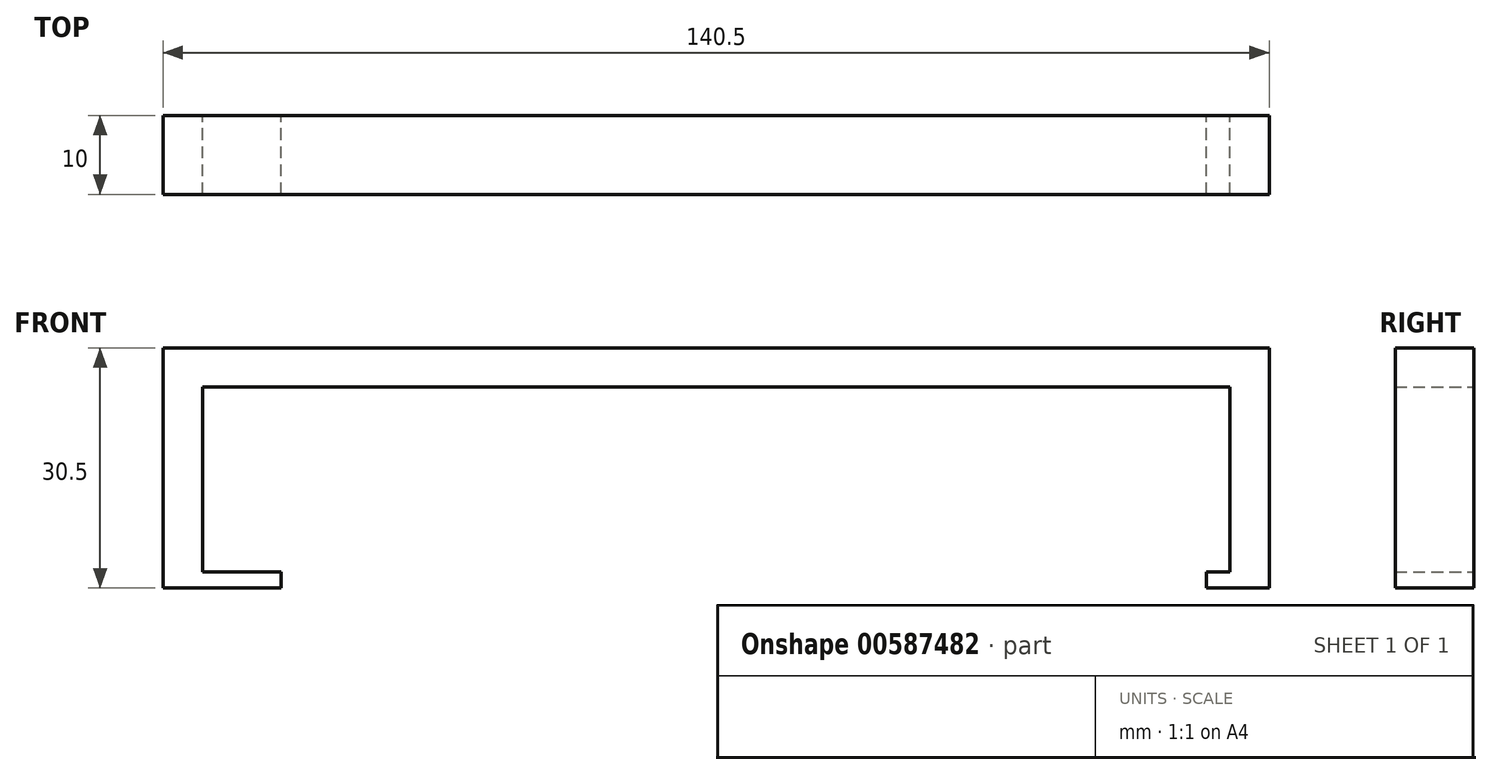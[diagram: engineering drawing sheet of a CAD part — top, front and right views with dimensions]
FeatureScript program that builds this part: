
annotation { "Feature Type Name" : "Feature", "Feature Type Description" : "" }
export const myFeature = defineFeature(function(context is Context, id is Id, definition is map)
    precondition{}
    {
        {
            var Q0;
            Q0=qCreatedBy(makeId("Front.planeOp"),FACE);
            var sketch = newSketch(context, id + "F0", { "sketchPlane" : qUnion([Q0])});
            skLineSegment(sketch, "E0.bottom", {"start": v(-65.25, 2.5) * mm, "end": v(65.25, 2.5) * mm});
            skLineSegment(sketch, "E0.top", {"start": v(-65.25, -2.5) * mm, "end": v(65.25, -2.5) * mm});
            skLineSegment(sketch, "E0.left", {"start": v(-65.25, 2.5) * mm, "end": v(-65.25, -2.5) * mm});
            skLineSegment(sketch, "E0.right", {"start": v(65.25, 2.5) * mm, "end": v(65.25, -2.5) * mm});
            skPoint(sketch, "E0.middle", {"position": v(0, 0) * mm});
            skLineSegment(sketch, "E1.top", {"start": v(65.27, -26) * mm, "end": v(70.25, -26) * mm});
            skLineSegment(sketch, "E2.bottom", {"start": v(70.25, -26) * mm, "end": v(62.25, -26) * mm});
            skLineSegment(sketch, "E2.top", {"start": v(70.25, -28) * mm, "end": v(62.25, -28) * mm});
            skLineSegment(sketch, "E2.left", {"start": v(70.25, -26) * mm, "end": v(70.25, -28) * mm});
            skLineSegment(sketch, "E2.right", {"start": v(62.25, -26) * mm, "end": v(62.25, -28) * mm});
            skLineSegment(sketch, "E3.bottom", {"start": v(-70.25, -26) * mm, "end": v(-55.25, -26) * mm});
            skLineSegment(sketch, "E3.top", {"start": v(-70.25, -28) * mm, "end": v(-55.25, -28) * mm});
            skLineSegment(sketch, "E3.left", {"start": v(-70.25, -26) * mm, "end": v(-70.25, -28) * mm});
            skLineSegment(sketch, "E3.right", {"start": v(-55.25, -26) * mm, "end": v(-55.25, -28) * mm});
            skLineSegment(sketch, "E4.bottom", {"start": v(-65.25, 2.5) * mm, "end": v(-70.25, 2.5) * mm});
            skLineSegment(sketch, "E4.top", {"start": v(-65.25, -26) * mm, "end": v(-70.25, -26) * mm});
            skLineSegment(sketch, "E4.left", {"start": v(-65.25, 2.5) * mm, "end": v(-65.25, -26) * mm});
            skLineSegment(sketch, "E4.right", {"start": v(-70.25, 2.5) * mm, "end": v(-70.25, -26) * mm});
            skLineSegment(sketch, "E5.bottom", {"start": v(65.25, 2.5) * mm, "end": v(70.25, 2.5) * mm});
            skLineSegment(sketch, "E5.top", {"start": v(65.25, -26) * mm, "end": v(70.25, -26) * mm});
            skLineSegment(sketch, "E5.left", {"start": v(65.25, 2.5) * mm, "end": v(65.25, -26) * mm});
            skLineSegment(sketch, "E5.right", {"start": v(70.25, 2.5) * mm, "end": v(70.25, -26) * mm});
            skSolve(sketch);
        }
        {
            var Q0;
            {var subQ1=sQuery(id+"F0.wireOp",EDGE,"E2.bottom");Q0=makeQuery(id+"F0.imprint","IMPRINT",FACE,{"disambiguationData":[TD([[makeQuery(id+"F0.imprint","IMPRINT",EDGE,{"derivedFrom":subQ1}),1.0]])]});}
            var Q1;
            {var subQ3=sQuery(id+"F0.wireOp",EDGE,"E4.bottom");Q1=makeQuery(id+"F0.imprint","IMPRINT",FACE,{"disambiguationData":[TD([[makeQuery(id+"F0.imprint","IMPRINT",EDGE,{"derivedFrom":subQ3}),1.0]])]});}
            var Q2;
            {var subQ1=sQuery(id+"F0.wireOp",EDGE,"E5.bottom");Q2=makeQuery(id+"F0.imprint","IMPRINT",FACE,{"disambiguationData":[TD([[makeQuery(id+"F0.imprint","IMPRINT",EDGE,{"derivedFrom":subQ1}),-1.0]])]});}
            var Q3;
            {var subQ0=sQuery(id+"F0.wireOp",EDGE,"E0.bottom");Q3=makeQuery(id+"F0.imprint","IMPRINT",FACE,{"disambiguationData":[TD([[makeQuery(id+"F0.imprint","IMPRINT",EDGE,{"derivedFrom":subQ0}),-1.0]])]});}
            var Q4;
            Q4=makeQuery(id+"F0.imprint","IMPRINT",FACE,{"disambiguationData":[TD([[makeQuery(id+"F0.imprint","IMPRINT",EDGE,{"derivedFrom":sQuery(id+"F0.wireOp",EDGE,"E3.bottom")}),-1.0]])]});
            extrude(context, id + "F1", {"entities" : qUnion([Q0, Q1, Q2, Q3, Q4]), "depth" : 10 * mm, "offsetDistance" : 25 * mm});
        }
    });
